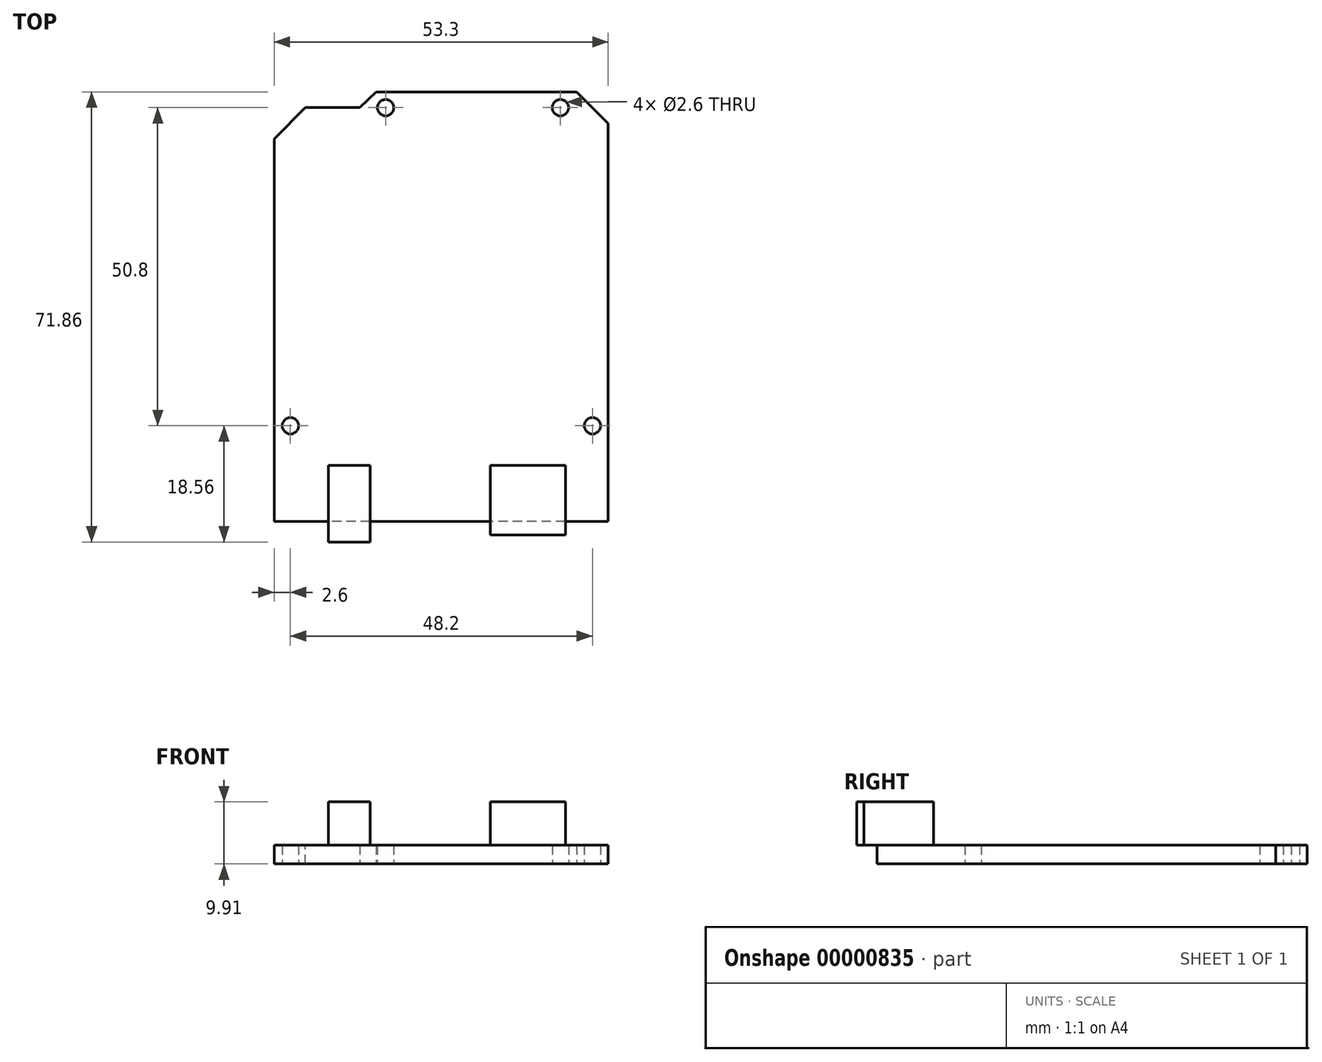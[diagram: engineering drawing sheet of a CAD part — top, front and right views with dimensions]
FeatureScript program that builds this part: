
annotation { "Feature Type Name" : "Feature", "Feature Type Description" : "" }
export const myFeature = defineFeature(function(context is Context, id is Id, definition is map)
    precondition{}
    {
        {
            var Q0;
            Q0=qCreatedBy(makeId("Top.planeOp"),FACE);
            var sketch = newSketch(context, id + "F0", { "sketchPlane" : qUnion([Q0])});
            skLineSegment(sketch, "E0.rect.bottom", {"start": v(26.65, -34.3) * mm, "end": v(-26.65, -34.3) * mm});
            skLineSegment(sketch, "E0.rect.top", {"start": v(26.65, 34.3) * mm, "end": v(-26.65, 34.3) * mm, "construction": true});
            skLineSegment(sketch, "E0.rect.left", {"start": v(26.65, -34.3) * mm, "end": v(26.65, 34.3) * mm});
            skLineSegment(sketch, "E0.rect.right", {"start": v(-26.65, -34.3) * mm, "end": v(-26.65, 34.3) * mm});
            skPoint(sketch, "E0.rect.middle", {"position": v(0, 0) * mm});
            skCircle(sketch, "E1", {"center": v(24.15, -19) * mm, "radius": 1.3 * mm});
            skCircle(sketch, "E2", {"center": v(-24.05, -19) * mm, "radius": 1.3 * mm});
            skLineSegment(sketch, "E3", {"start": v(26.65, 34.3) * mm, "end": v(-10.4, 34.3) * mm});
            skLineSegment(sketch, "E4", {"start": v(-10.4, 34.3) * mm, "end": v(-12.98, 31.8) * mm});
            skLineSegment(sketch, "E5", {"start": v(-12.98, 31.8) * mm, "end": v(-26.65, 31.8) * mm});
            skCircle(sketch, "E6", {"center": v(19.05, 31.8) * mm, "radius": 1.3 * mm});
            skCircle(sketch, "E7", {"center": v(-8.85, 31.8) * mm, "radius": 1.3 * mm});
            skSolve(sketch);
        }
        {
            var Q0;
            {var subQ2=sQuery(id+"F0.wireOp",EDGE,"E0.rect.bottom");Q0=makeQuery(id+"F0.imprint","IMPRINT",FACE,{"disambiguationData":[TD([[makeQuery(id+"F0.imprint","IMPRINT",EDGE,{"derivedFrom":subQ2}),-1.0]])]});}
            extrude(context, id + "F1", {"entities" : qUnion([Q0]), "depth" : 3 * mm});
        }
        {
            var Q0;
            Q0=makeQuery(id+"F1.opExtrude","CAP_FACE",FACE,{"disambiguationData":[OSD([sQuery(id+"F0.wireOp",EDGE,"E0.rect.bottom"),sQuery(id+"F0.wireOp",EDGE,"E0.rect.left"),sQuery(id+"F0.wireOp",EDGE,"E0.rect.right"),sQuery(id+"F0.wireOp",EDGE,"E1"),sQuery(id+"F0.wireOp",EDGE,"E2"),sQuery(id+"F0.wireOp",EDGE,"E3"),sQuery(id+"F0.wireOp",EDGE,"E4"),sQuery(id+"F0.wireOp",EDGE,"E5"),sQuery(id+"F0.wireOp",EDGE,"E6"),sQuery(id+"F0.wireOp",EDGE,"E7")])],"isStart":false});
            var sketch = newSketch(context, id + "F2", { "sketchPlane" : qUnion([Q0])});
            skSolve(sketch);
        }
        {
            var Q0;
            Q0=makeQuery(id+"F1.opExtrude","SWEPT_EDGE",EDGE,{"disambiguationData":[OSD([sQuery(id+"F0.wireOp",EDGE,"E0.rect.left"),sQuery(id+"F0.wireOp",EDGE,"E3")])]});
            chamfer(context, id + "F3", {"entities" : qUnion([Q0]), "width" : 5 * mm, "tangentPropagation" : true});
        }
        {
            var Q0;
            Q0=makeQuery(id+"F1.opExtrude","SWEPT_EDGE",EDGE,{"disambiguationData":[OSD([sQuery(id+"F0.wireOp",EDGE,"E0.rect.right"),sQuery(id+"F0.wireOp",EDGE,"E5")])]});
            chamfer(context, id + "F4", {"entities" : qUnion([Q0]), "width" : 5 * mm, "tangentPropagation" : true});
        }
        {
            var Q0;
            Q0=makeQuery(id+"F2.imprint","IMPRINT",FACE,{"disambiguationData":[TD([[makeQuery(id+"F2.imprint","IMPRINT",EDGE,{"derivedFrom":makeQuery(id+"F1.opExtrude","CAP_EDGE",EDGE,{"disambiguationData":[OSD([sQuery(id+"F0.wireOp",EDGE,"E0.rect.bottom")])],"isStart":false})}),-1.0]])]});
            var sketch = newSketch(context, id + "F5", { "sketchPlane" : qUnion([Q0])});
            skLineSegment(sketch, "E8.bottom", {"start": v(19.83, -25.31) * mm, "end": v(7.86, -25.31) * mm});
            skLineSegment(sketch, "E8.top", {"start": v(19.83, -36.4) * mm, "end": v(7.86, -36.4) * mm});
            skLineSegment(sketch, "E8.left", {"start": v(19.83, -25.31) * mm, "end": v(19.83, -36.4) * mm});
            skLineSegment(sketch, "E8.right", {"start": v(7.86, -25.31) * mm, "end": v(7.86, -36.4) * mm});
            skLineSegment(sketch, "E9.bottom", {"start": v(-11.31, -25.31) * mm, "end": v(-17.96, -25.31) * mm});
            skLineSegment(sketch, "E9.top", {"start": v(-11.31, -37.56) * mm, "end": v(-17.96, -37.56) * mm});
            skLineSegment(sketch, "E9.left", {"start": v(-11.31, -25.31) * mm, "end": v(-11.31, -37.56) * mm});
            skLineSegment(sketch, "E9.right", {"start": v(-17.96, -25.31) * mm, "end": v(-17.96, -37.56) * mm});
            skLineSegment(sketch, "E10", {"start": v(-32.29, -25.31) * mm, "end": v(35.9, -25.31) * mm, "construction": true});
            skSolve(sketch);
        }
        {
            var Q0;
            {var subQ3=sQuery(id+"F5.wireOp",EDGE,"E8.top");var subQ12=sQuery(id+"F5.wireOp",EDGE,"E9.top");var subQ13=sQuery(id+"F5.wireOp",EDGE,"E8.bottom");var subQ14=sQuery(id+"F5.wireOp",EDGE,"E9.bottom");Q0=qUnion([makeQuery(id+"F5.imprint","IMPRINT",FACE,{"disambiguationData":[TD([[makeQuery(id+"F5.imprint","IMPRINT",EDGE,{"derivedFrom":subQ3}),-1.0]])]}),makeQuery(id+"F5.imprint","IMPRINT",FACE,{"disambiguationData":[TD([[makeQuery(id+"F5.imprint","IMPRINT",EDGE,{"derivedFrom":subQ12}),-1.0]])]}),makeQuery(id+"F5.imprint","IMPRINT",FACE,{"disambiguationData":[TD([[makeQuery(id+"F5.imprint","IMPRINT",EDGE,{"derivedFrom":subQ13}),1.0]])]}),makeQuery(id+"F5.imprint","IMPRINT",FACE,{"disambiguationData":[TD([[makeQuery(id+"F5.imprint","IMPRINT",EDGE,{"derivedFrom":subQ14}),1.0]])]})]);}
            extrude(context, id + "F6", {"entities" : qUnion([Q0]), "depth" : 6.93 * mm});
        }
    });
